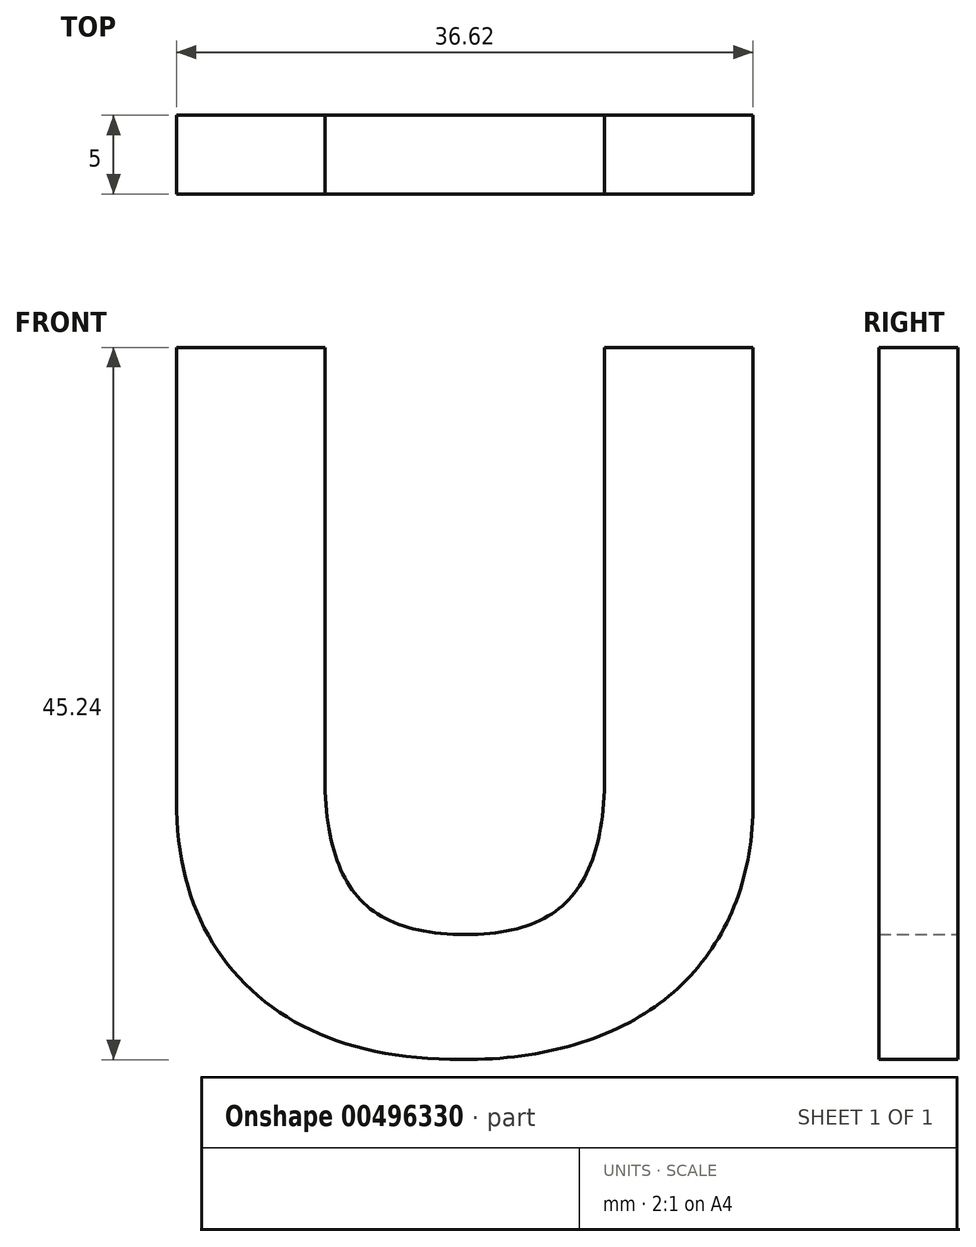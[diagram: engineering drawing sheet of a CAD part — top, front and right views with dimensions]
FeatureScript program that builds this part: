
annotation { "Feature Type Name" : "Feature", "Feature Type Description" : "" }
export const myFeature = defineFeature(function(context is Context, id is Id, definition is map)
    precondition{}
    {
        {
            var Q0;
            Q0=qCreatedBy(makeId("Front.planeOp"),FACE);
            var sketch = newSketch(context, id + "F0", { "sketchPlane" : qUnion([Q0])});
            skText(sketch, "E0", { "text": "U", "fontName": "OpenSans-Bold.ttf"});
            const initialGuessF0  = {"E0": [-0.06612, 0.01177, 1, 0, 0.045]};
            skSetInitialGuess(sketch, initialGuessF0);
            skSolve(sketch);
        }
        {
            var Q0;
            Q0=makeQuery(id+"F0.imprint","IMPRINT",FACE,{"disambiguationData":[TD([[makeQuery(id+"F0.imprint","IMPRINT",EDGE,{"derivedFrom":sQuery(id+"F0.wireOp",EDGE,"E0.sketch_text.stroke-0")}),-1.0]])]});
            extrude(context, id + "F1", {"entities" : qUnion([Q0]), "depth" : 5 * mm});
        }
    });
